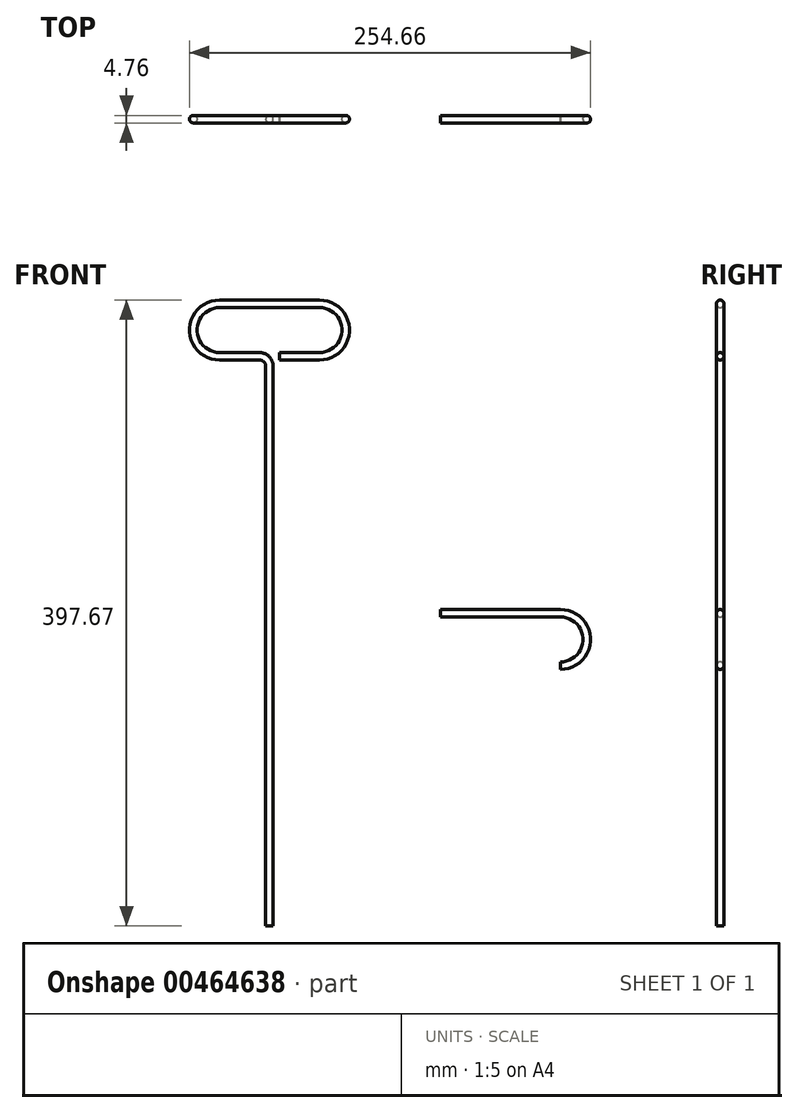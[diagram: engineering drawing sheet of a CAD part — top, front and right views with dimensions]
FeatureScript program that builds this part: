
annotation { "Feature Type Name" : "Feature", "Feature Type Description" : "" }
export const myFeature = defineFeature(function(context is Context, id is Id, definition is map)
    precondition{}
    {
        {
            var Q0;
            Q0=qCreatedBy(makeId("Front.planeOp"),FACE);
            var sketch = newSketch(context, id + "F0", { "sketchPlane" : qUnion([Q0])});
            skArc(sketch, "E0", {"start": v(-83.42, 55.95) * mm, "mid": v(-100.09, 39.29) * mm, "end": v(-83.42, 22.62) * mm});
            skArc(sketch, "E1", {"start": v(-19.92, 22.62) * mm, "mid": v(-3.25, 39.29) * mm, "end": v(-19.92, 55.95) * mm});
            skLineSegment(sketch, "E2", {"start": v(-83.42, 55.95) * mm, "end": v(-19.92, 55.95) * mm});
            skLineSegment(sketch, "E3", {"start": v(-83.42, 22.62) * mm, "end": v(-58.02, 22.62) * mm});
            skLineSegment(sketch, "E4", {"start": v(-51.67, 16.27) * mm, "end": v(-51.67, -339.33) * mm});
            skLineSegment(sketch, "E5", {"start": v(-19.92, 22.62) * mm, "end": v(-45.32, 22.62) * mm});
            skPoint(sketch, "E6.visualSharp", {"position": v(-51.67, 22.62) * mm});
            skArc(sketch, "E6.filletArc", {"start": v(-51.67, 16.27) * mm, "mid": v(-53.53, 20.76) * mm, "end": v(-58.02, 22.62) * mm});
            skPoint(sketch, "E7.orphan", {"position": v(-51.67, 55.95) * mm});
            skArc(sketch, "E8", {"start": v(133.14, -173.92) * mm, "mid": v(149.8, -157.25) * mm, "end": v(133.14, -140.59) * mm});
            skLineSegment(sketch, "E9", {"start": v(56.94, -140.59) * mm, "end": v(133.14, -140.59) * mm});
            skSolve(sketch);
        }
        {
            var Q0;
            Q0=sQuery(id+"F0.wireOp",VERTEX,"E4.end");
            var Q1;
            Q1=sQuery(id+"F0.wireOp",EDGE,"E4");
            cPlane(context, id + "F1", {"entities" : qUnion([Q0, Q1]), "cplaneType" : CPlaneType.LINE_POINT, "offset" : 25.4 * mm, "width" : 152.4 * mm, "height" : 152.4 * mm});
        }
        {
            var Q0;
            Q0=qCreatedBy(id+"F1.planeOp",FACE);
            var sketch = newSketch(context, id + "F2", { "sketchPlane" : qUnion([Q0])});
            skCircle(sketch, "E10", {"center": v(-51.67, 0) * mm, "radius": 2.38 * mm});
            skSolve(sketch);
        }
        {
            var Q0;
            Q0=makeQuery(id+"F2.imprint","IMPRINT",FACE,{"disambiguationData":[TD([[makeQuery(id+"F2.imprint","IMPRINT",EDGE,{"derivedFrom":sQuery(id+"F2.wireOp",EDGE,"E10")}),1.0]])]});
            var Q1;
            Q1=sQuery(id+"F0.wireOp",EDGE,"E4");
            var Q2;
            Q2=sQuery(id+"F0.wireOp",EDGE,"E6.filletArc");
            var Q3;
            Q3=sQuery(id+"F0.wireOp",EDGE,"E3");
            var Q4;
            Q4=sQuery(id+"F0.wireOp",EDGE,"E0");
            var Q5;
            Q5=sQuery(id+"F0.wireOp",EDGE,"E2");
            var Q6;
            Q6=sQuery(id+"F0.wireOp",EDGE,"E1");
            var Q7;
            Q7=sQuery(id+"F0.wireOp",EDGE,"E5");
            sweep(context, id + "F3", {"profiles" : qUnion([Q0]), "path" : qUnion([Q1, Q2, Q3, Q4, Q5, Q6, Q7])});
        }
        {
            var Q0;
            Q0=sQuery(id+"F0.wireOp",VERTEX,"E9.start");
            var Q1;
            Q1=sQuery(id+"F0.wireOp",EDGE,"E9");
            cPlane(context, id + "F4", {"entities" : qUnion([Q0, Q1]), "cplaneType" : CPlaneType.LINE_POINT, "offset" : 25.4 * mm, "width" : 152.4 * mm, "height" : 152.4 * mm});
        }
        {
            var Q0;
            Q0=qCreatedBy(id+"F4.planeOp",FACE);
            var sketch = newSketch(context, id + "F5", { "sketchPlane" : qUnion([Q0])});
            skCircle(sketch, "E11", {"center": v(0, -140.59) * mm, "radius": 2.38 * mm});
            skSolve(sketch);
        }
        {
            var Q0;
            Q0=makeQuery(id+"F5.imprint","IMPRINT",FACE,{"disambiguationData":[TD([[makeQuery(id+"F5.imprint","IMPRINT",EDGE,{"derivedFrom":sQuery(id+"F5.wireOp",EDGE,"E11")}),1.0]])]});
            var Q1;
            Q1=sQuery(id+"F0.wireOp",EDGE,"E9");
            var Q2;
            Q2=sQuery(id+"F0.wireOp",EDGE,"E8");
            sweep(context, id + "F6", {"profiles" : qUnion([Q0]), "path" : qUnion([Q1, Q2])});
        }
    });
